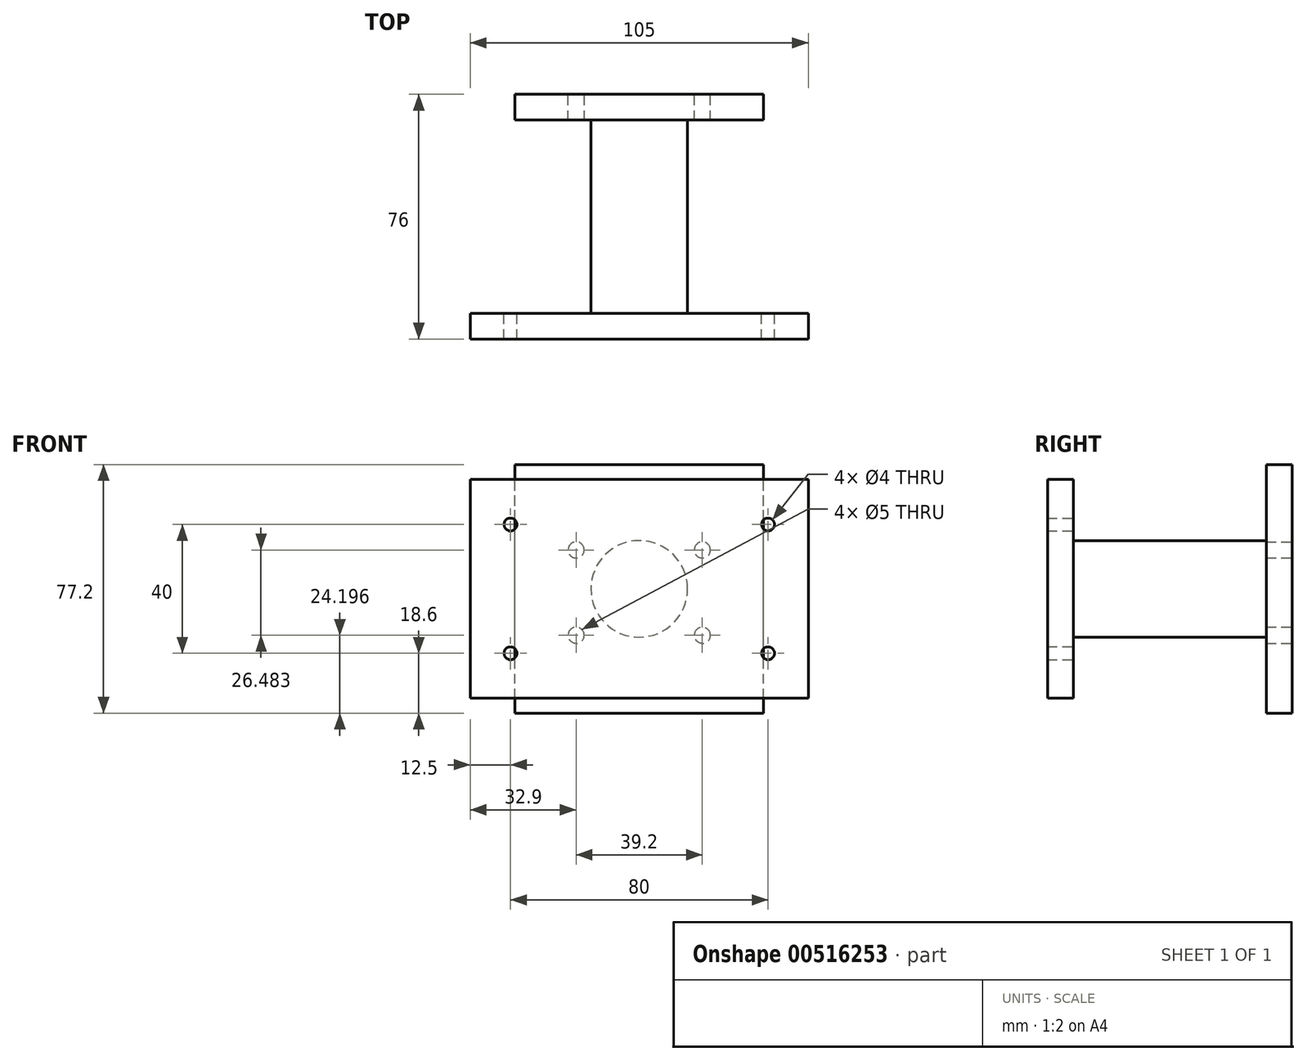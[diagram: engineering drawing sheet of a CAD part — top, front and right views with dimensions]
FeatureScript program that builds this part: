
annotation { "Feature Type Name" : "Feature", "Feature Type Description" : "" }
export const myFeature = defineFeature(function(context is Context, id is Id, definition is map)
    precondition{}
    {
        {
            var Q0;
            Q0=qCreatedBy(makeId("Front.planeOp"),FACE);
            var sketch = newSketch(context, id + "F0", { "sketchPlane" : qUnion([Q0])});
            skLineSegment(sketch, "E0.bottom", {"start": v(52.5, -34) * mm, "end": v(-52.5, -34) * mm});
            skLineSegment(sketch, "E0.top", {"start": v(52.5, 34) * mm, "end": v(-52.5, 34) * mm});
            skLineSegment(sketch, "E0.left", {"start": v(52.5, -34) * mm, "end": v(52.5, 34) * mm});
            skLineSegment(sketch, "E0.right", {"start": v(-52.5, -34) * mm, "end": v(-52.5, 34) * mm});
            skPoint(sketch, "E0.middle", {"position": v(0, 0) * mm});
            skCircle(sketch, "E1", {"center": v(-40, 20) * mm, "radius": 2 * mm});
            skCircle(sketch, "E2", {"center": v(-40, -20) * mm, "radius": 2 * mm});
            skCircle(sketch, "E3", {"center": v(40, -20) * mm, "radius": 2 * mm});
            skCircle(sketch, "E4", {"center": v(40, 20) * mm, "radius": 2 * mm});
            skSolve(sketch);
        }
        {
            var Q0;
            Q0=makeQuery(id+"F0.imprint","IMPRINT",FACE,{"disambiguationData":[TD([[makeQuery(id+"F0.imprint","IMPRINT",EDGE,{"derivedFrom":sQuery(id+"F0.wireOp",EDGE,"E0.bottom")}),-1.0]])]});
            extrude(context, id + "F1", {"entities" : qUnion([Q0]), "depth" : 8 * mm, "offsetDistance" : 25 * mm});
        }
        {
            var Q0;
            Q0=qCreatedBy(makeId("Front.planeOp"),FACE);
            var sketch = newSketch(context, id + "F2", { "sketchPlane" : qUnion([Q0])});
            skCircle(sketch, "E5", {"center": v(0, 0) * mm, "radius": 15 * mm});
            skSolve(sketch);
        }
        {
            var Q0;
            Q0 = qSketchRegion(id + "F2", true);
            extrude(context, id + "F3", {"entities" : qUnion([Q0]), "operationType" : NewBodyOperationType.ADD, "oppositeDirection" : true, "depth" : 60 * mm, "offsetDistance" : 25 * mm});
        }
        {
            var Q0;
            Q0=makeQuery(id+"F3.opExtrude","CAP_FACE",FACE,{"disambiguationData":[OSD([sQuery(id+"F2.wireOp",EDGE,"E5")])],"isStart":false});
            var sketch = newSketch(context, id + "F4", { "sketchPlane" : qUnion([Q0])});
            skLineSegment(sketch, "E6.bottom", {"start": v(38.6, -38.6) * mm, "end": v(-38.6, -38.6) * mm});
            skLineSegment(sketch, "E6.top", {"start": v(38.6, 38.6) * mm, "end": v(-38.6, 38.6) * mm});
            skLineSegment(sketch, "E6.left", {"start": v(38.6, -38.6) * mm, "end": v(38.6, 38.6) * mm});
            skLineSegment(sketch, "E6.right", {"start": v(-38.6, -38.6) * mm, "end": v(-38.6, 38.6) * mm});
            skPoint(sketch, "E6.middle", {"position": v(0, 0) * mm});
            skSolve(sketch);
        }
        {
            var Q0;
            Q0 = qSketchRegion(id + "F4", true);
            extrude(context, id + "F5", {"entities" : qUnion([Q0]), "operationType" : NewBodyOperationType.ADD, "depth" : 8 * mm, "offsetDistance" : 25 * mm});
        }
        {
            var Q0;
            Q0=makeQuery(id+"F5.opExtrude","CAP_FACE",FACE,{"disambiguationData":[OSD([sQuery(id+"F4.wireOp",EDGE,"E6.bottom"),sQuery(id+"F4.wireOp",EDGE,"E6.top"),sQuery(id+"F4.wireOp",EDGE,"E6.left"),sQuery(id+"F4.wireOp",EDGE,"E6.right")])],"isStart":false});
            var sketch = newSketch(context, id + "F6", { "sketchPlane" : qUnion([Q0])});
            skCircle(sketch, "E7", {"center": v(-19.6, 12.08) * mm, "radius": 2.5 * mm});
            skCircle(sketch, "E8", {"center": v(-19.6, -14.4) * mm, "radius": 2.5 * mm});
            skCircle(sketch, "E9", {"center": v(19.6, -14.4) * mm, "radius": 2.5 * mm});
            skCircle(sketch, "E10", {"center": v(19.6, 12.08) * mm, "radius": 2.5 * mm});
            skSolve(sketch);
        }
        {
            var Q0;
            Q0 = qSketchRegion(id + "F6", true);
            extrude(context, id + "F7", {"entities" : qUnion([Q0]), "operationType" : NewBodyOperationType.REMOVE, "oppositeDirection" : true, "depth" : 44.4 * mm, "offsetDistance" : 25 * mm});
        }
    });
